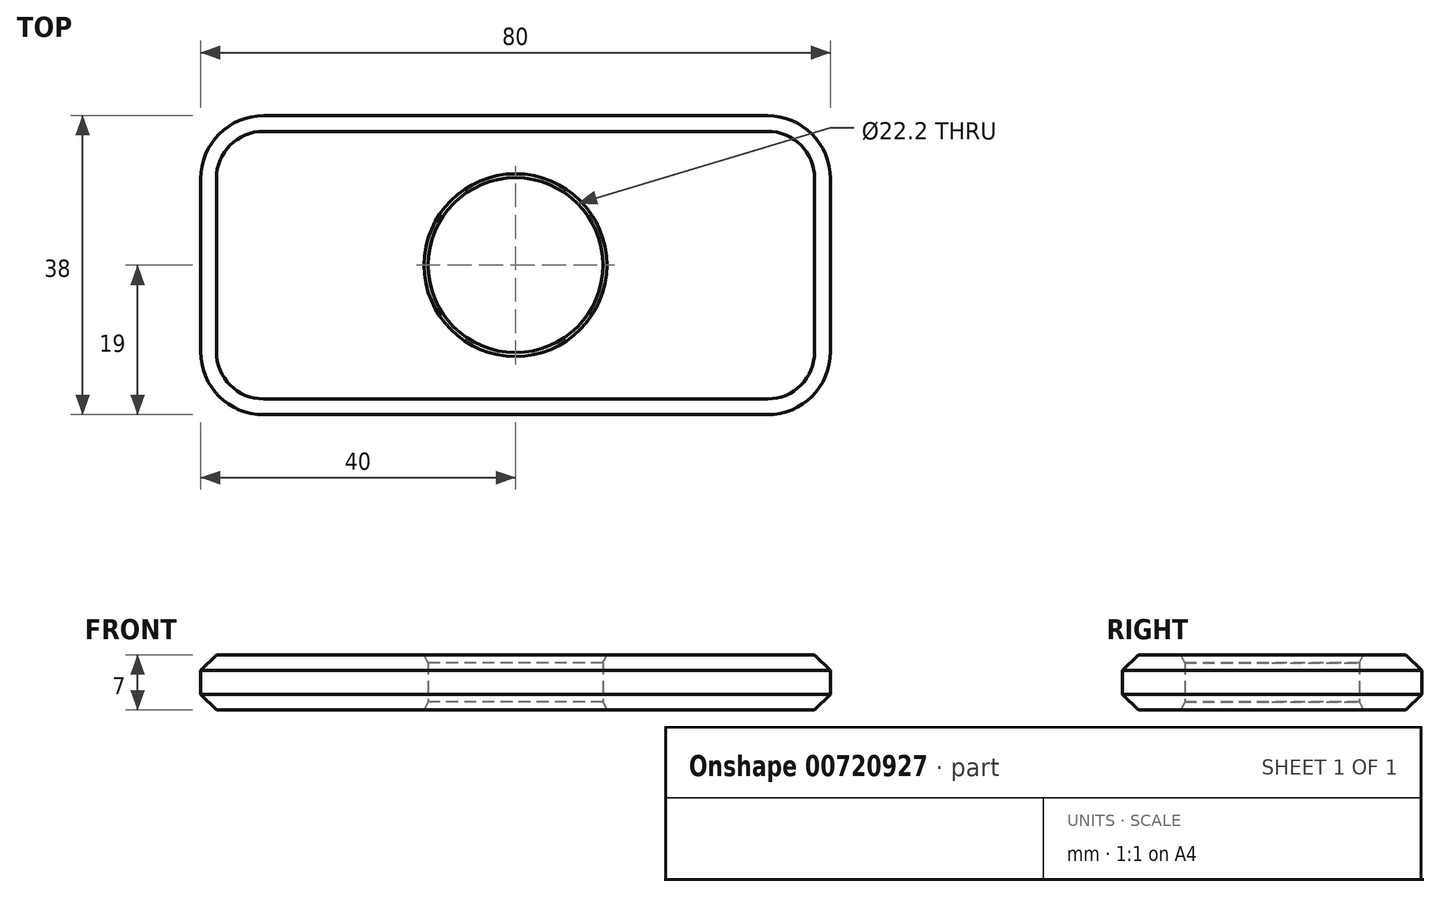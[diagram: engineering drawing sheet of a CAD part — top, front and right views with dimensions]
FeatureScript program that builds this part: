
annotation { "Feature Type Name" : "Feature", "Feature Type Description" : "" }
export const myFeature = defineFeature(function(context is Context, id is Id, definition is map)
    precondition{}
    {
        {
            var Q0;
            Q0=qCreatedBy(makeId("Top.planeOp"),FACE);
            var sketch = newSketch(context, id + "F0", { "sketchPlane" : qUnion([Q0])});
            skCircle(sketch, "E0", {"center": v(0, 0) * mm, "radius": 11.1 * mm});
            skLineSegment(sketch, "E1.bottom", {"start": v(32, -19) * mm, "end": v(-32, -19) * mm});
            skLineSegment(sketch, "E1.top", {"start": v(32, 19) * mm, "end": v(-32, 19) * mm});
            skLineSegment(sketch, "E1.left", {"start": v(40, -11) * mm, "end": v(40, 11) * mm});
            skLineSegment(sketch, "E1.right", {"start": v(-40, -11) * mm, "end": v(-40, 11) * mm});
            skPoint(sketch, "E2.visualSharp", {"position": v(-40, 19) * mm});
            skArc(sketch, "E2.filletArc", {"start": v(-32, 19) * mm, "mid": v(-37.66, 16.66) * mm, "end": v(-40, 11) * mm});
            skPoint(sketch, "E3.visualSharp", {"position": v(-40, -19) * mm});
            skArc(sketch, "E3.filletArc", {"start": v(-40, -11) * mm, "mid": v(-37.66, -16.66) * mm, "end": v(-32, -19) * mm});
            skPoint(sketch, "E4.visualSharp", {"position": v(40, 19) * mm});
            skArc(sketch, "E4.filletArc", {"start": v(40, 11) * mm, "mid": v(37.66, 16.66) * mm, "end": v(32, 19) * mm});
            skPoint(sketch, "E5.visualSharp", {"position": v(40, -19) * mm});
            skArc(sketch, "E5.filletArc", {"start": v(32, -19) * mm, "mid": v(37.66, -16.66) * mm, "end": v(40, -11) * mm});
            skSolve(sketch);
        }
        {
            var Q0;
            Q0=qSketchRegion(id+"F0",true);
            extrude(context, id + "F1", {"entities" : qUnion([Q0]), "depth" : 7 * mm});
        }
        {
            var Q0;
            Q0=makeQuery(id+"F1.opExtrude","CAP_EDGE",EDGE,{"disambiguationData":[OSD([sQuery(id+"F0.wireOp",EDGE,"E1.bottom")])],"isStart":false});
            var Q1;
            Q1=makeQuery(id+"F1.opExtrude","CAP_EDGE",EDGE,{"disambiguationData":[OSD([sQuery(id+"F0.wireOp",EDGE,"E1.bottom")])],"isStart":true});
            chamfer(context, id + "F2", {"entities" : qUnion([Q0, Q1]), "width" : 2 * mm, "tangentPropagation" : true});
        }
        {
            var Q0;
            Q0=makeQuery(id+"F1.opExtrude","CAP_EDGE",EDGE,{"disambiguationData":[OSD([sQuery(id+"F0.wireOp",EDGE,"E0")])],"isStart":false});
            var Q1;
            Q1=makeQuery(id+"F1.opExtrude","CAP_EDGE",EDGE,{"disambiguationData":[OSD([sQuery(id+"F0.wireOp",EDGE,"E0")])],"isStart":true});
            chamfer(context, id + "F3", {"entities" : qUnion([Q0, Q1]), "chamferType" : ChamferType.TWO_OFFSETS, "width1" : 1 * mm, "oppositeDirection" : false, "width2" : .5 * mm, "tangentPropagation" : true});
        }
    });
